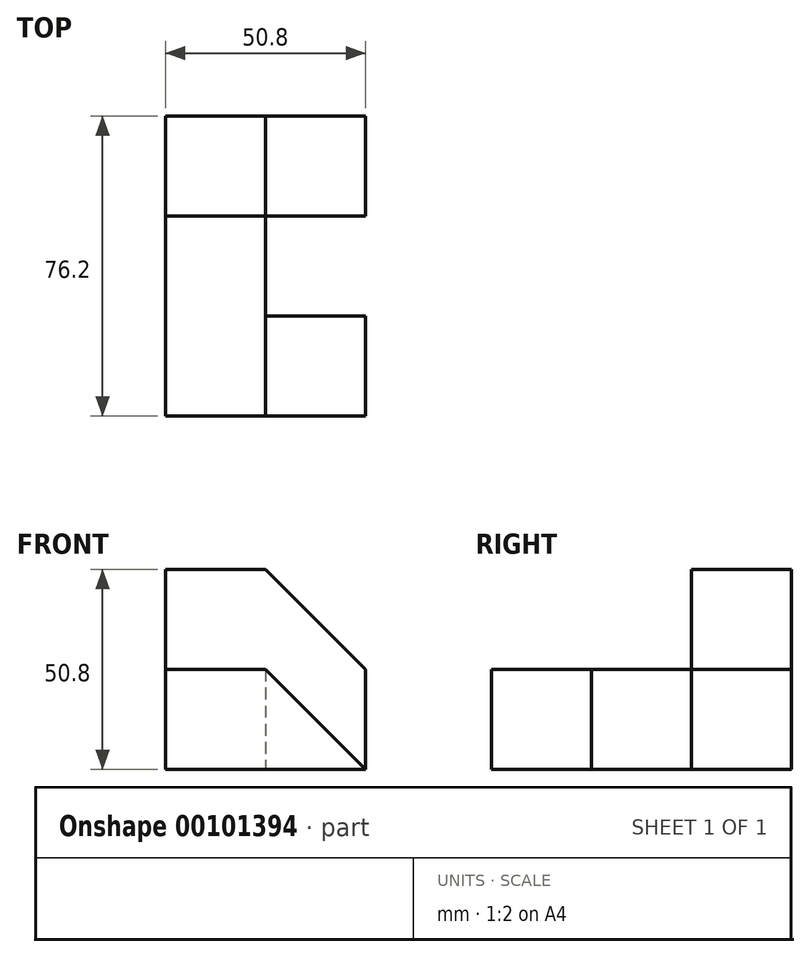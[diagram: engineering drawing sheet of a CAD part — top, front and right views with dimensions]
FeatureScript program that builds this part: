
annotation { "Feature Type Name" : "Feature", "Feature Type Description" : "" }
export const myFeature = defineFeature(function(context is Context, id is Id, definition is map)
    precondition{}
    {
        {
            var Q0;
            Q0=qCreatedBy(makeId("Front.planeOp"),FACE);
            var sketch = newSketch(context, id + "F0", { "sketchPlane" : qUnion([Q0])});
            skLineSegment(sketch, "E0", {"start": v(0, 0) * mm, "end": v(0, 25.4) * mm});
            skLineSegment(sketch, "E1", {"start": v(0, 0) * mm, "end": v(50.8, 0) * mm});
            skLineSegment(sketch, "E2", {"start": v(0, 50.8) * mm, "end": v(25.4, 50.8) * mm});
            skLineSegment(sketch, "E3", {"start": v(25.4, 50.8) * mm, "end": v(50.8, 25.4) * mm});
            skLineSegment(sketch, "E4", {"start": v(50.8, 25.4) * mm, "end": v(50.8, 0) * mm});
            skLineSegment(sketch, "E5", {"start": v(0, 50.8) * mm, "end": v(0, 25.4) * mm});
            skSolve(sketch);
        }
        {
            var Q0;
            Q0=qCreatedBy(makeId("Right.planeOp"),FACE);
            var sketch = newSketch(context, id + "F1", { "sketchPlane" : qUnion([Q0])});
            skLineSegment(sketch, "E6", {"start": v(50.8, 50.8) * mm, "end": v(50.8, 25.4) * mm});
            skLineSegment(sketch, "E7", {"start": v(50.8, 25.4) * mm, "end": v(0, 25.4) * mm});
            skLineSegment(sketch, "E8", {"start": v(25.4, 25.4) * mm, "end": v(50.8, 25.4) * mm});
            skLineSegment(sketch, "E9", {"start": v(0, 25.4) * mm, "end": v(0, 50.8) * mm});
            skLineSegment(sketch, "E10", {"start": v(0, 50.8) * mm, "end": v(50.8, 50.8) * mm});
            skSolve(sketch);
        }
        {
            var Q0;
            Q0 = qSketchRegion(id + "F0", true);
            extrude(context, id + "F2", {"entities" : qUnion([Q0]), "oppositeDirection" : true, "depth" : 76.2 * mm});
        }
        {
            var Q0;
            Q0 = qSketchRegion(id + "F1", true);
            extrude(context, id + "F3", {"entities" : qUnion([Q0]), "operationType" : NewBodyOperationType.REMOVE, "depth" : 50.8 * mm});
        }
        {
            var Q0;
            Q0=qCreatedBy(makeId("Top.planeOp"),FACE);
            var sketch = newSketch(context, id + "F4", { "sketchPlane" : qUnion([Q0])});
            skLineSegment(sketch, "E11", {"start": v(0, 50.8) * mm, "end": v(50.8, 50.8) * mm});
            skLineSegment(sketch, "E12", {"start": v(50.8, 50.8) * mm, "end": v(50.8, 25.4) * mm});
            skLineSegment(sketch, "E13", {"start": v(50.8, 25.4) * mm, "end": v(25.44, 25.4) * mm});
            skLineSegment(sketch, "E14", {"start": v(25.44, 25.4) * mm, "end": v(25.44, 50.8) * mm});
            skSolve(sketch);
        }
        {
            var Q0;
            Q0 = qSketchRegion(id + "F4", true);
            extrude(context, id + "F5", {"entities" : qUnion([Q0]), "operationType" : NewBodyOperationType.REMOVE, "depth" : 25.4 * mm});
        }
        {
            var Q0;
            Q0=makeQuery(id+"F2.opExtrude","CAP_FACE",FACE,{"disambiguationData":[OSD([sQuery(id+"F0.wireOp",EDGE,"E0"),sQuery(id+"F0.wireOp",EDGE,"E1"),sQuery(id+"F0.wireOp",EDGE,"E2"),sQuery(id+"F0.wireOp",EDGE,"E3"),sQuery(id+"F0.wireOp",EDGE,"E4"),sQuery(id+"F0.wireOp",EDGE,"E5")])],"isStart":true});
            var sketch = newSketch(context, id + "F6", { "sketchPlane" : qUnion([Q0])});
            skLineSegment(sketch, "E15", {"start": v(50.8, 0) * mm, "end": v(25.4, 25.4) * mm});
            skLineSegment(sketch, "E16", {"start": v(25.4, 25.4) * mm, "end": v(50.8, 25.4) * mm});
            skLineSegment(sketch, "E17", {"start": v(50.8, 25.4) * mm, "end": v(50.8, 0) * mm});
            skSolve(sketch);
        }
        {
            var Q0;
            Q0 = qSketchRegion(id + "F6", true);
            extrude(context, id + "F7", {"entities" : qUnion([Q0]), "operationType" : NewBodyOperationType.REMOVE, "oppositeDirection" : true, "depth" : 25.4 * mm});
        }
    });
